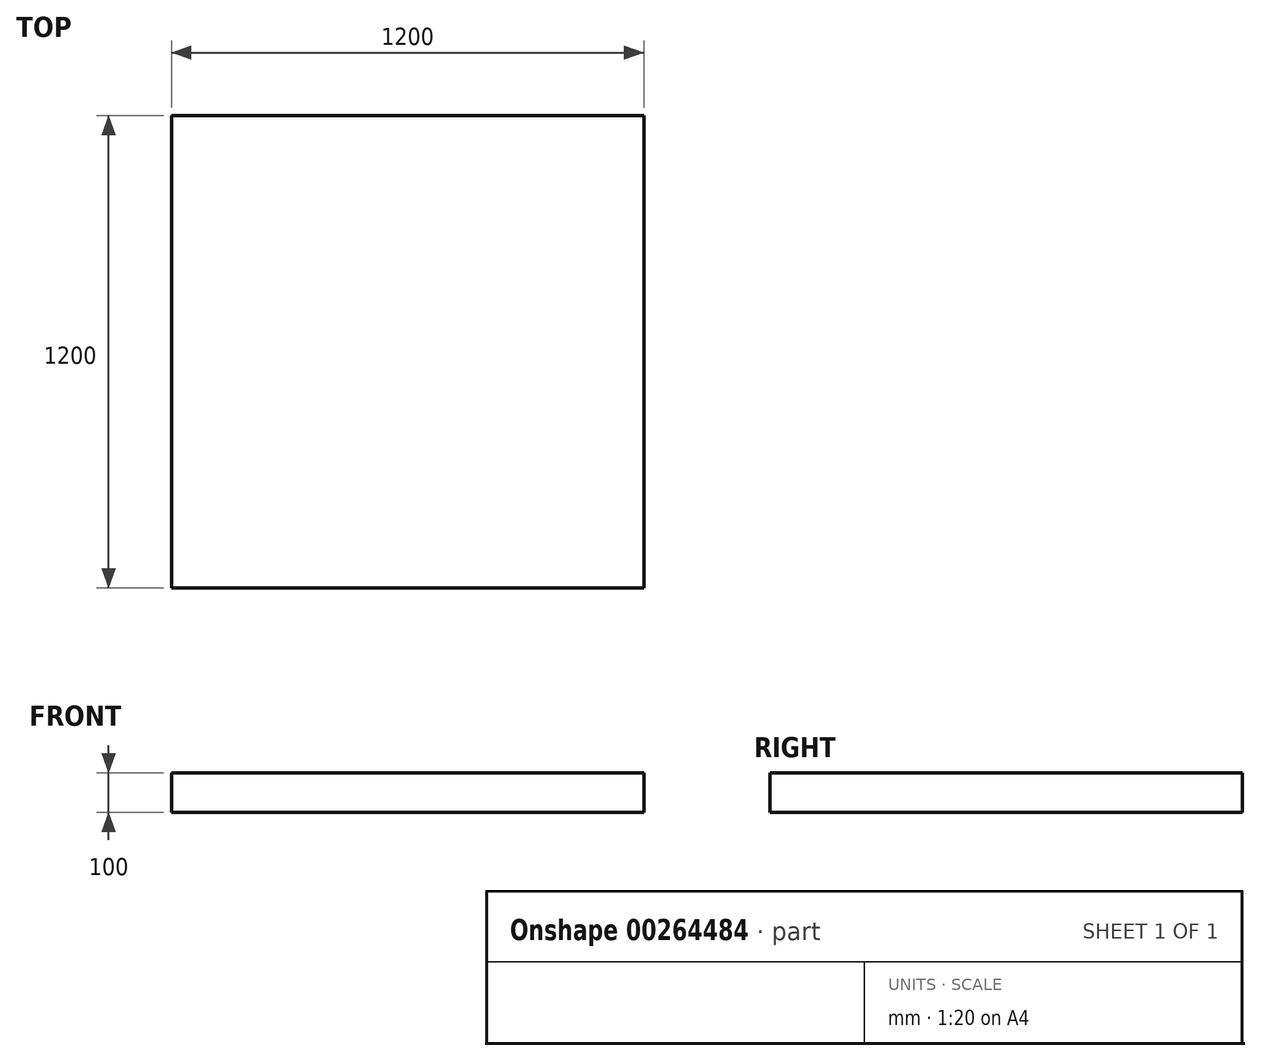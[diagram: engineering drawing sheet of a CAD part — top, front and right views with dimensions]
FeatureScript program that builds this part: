
annotation { "Feature Type Name" : "Feature", "Feature Type Description" : "" }
export const myFeature = defineFeature(function(context is Context, id is Id, definition is map)
    precondition{}
    {
        {
            var Q0;
            Q0=qCreatedBy(makeId("Top.planeOp"),FACE);
            var sketch = newSketch(context, id + "F0", { "sketchPlane" : qUnion([Q0])});
            skLineSegment(sketch, "E0.bottom", {"start": v(-600, 600) * mm, "end": v(600, 600) * mm});
            skLineSegment(sketch, "E0.top", {"start": v(-600, -600) * mm, "end": v(600, -600) * mm});
            skLineSegment(sketch, "E0.left", {"start": v(-600, 600) * mm, "end": v(-600, -600) * mm});
            skLineSegment(sketch, "E0.right", {"start": v(600, 600) * mm, "end": v(600, -600) * mm});
            skLineSegment(sketch, "E1", {"start": v(0, 0) * mm, "end": v(0, 600) * mm, "construction": true});
            skLineSegment(sketch, "E2", {"start": v(0, 0) * mm, "end": v(-600, 0) * mm, "construction": true});
            skSolve(sketch);
        }
        {
            var Q0;
            Q0 = qSketchRegion(id + "F0", true);
            extrude(context, id + "F1", {"entities" : qUnion([Q0]), "depth" : 100 * mm});
        }
    });
